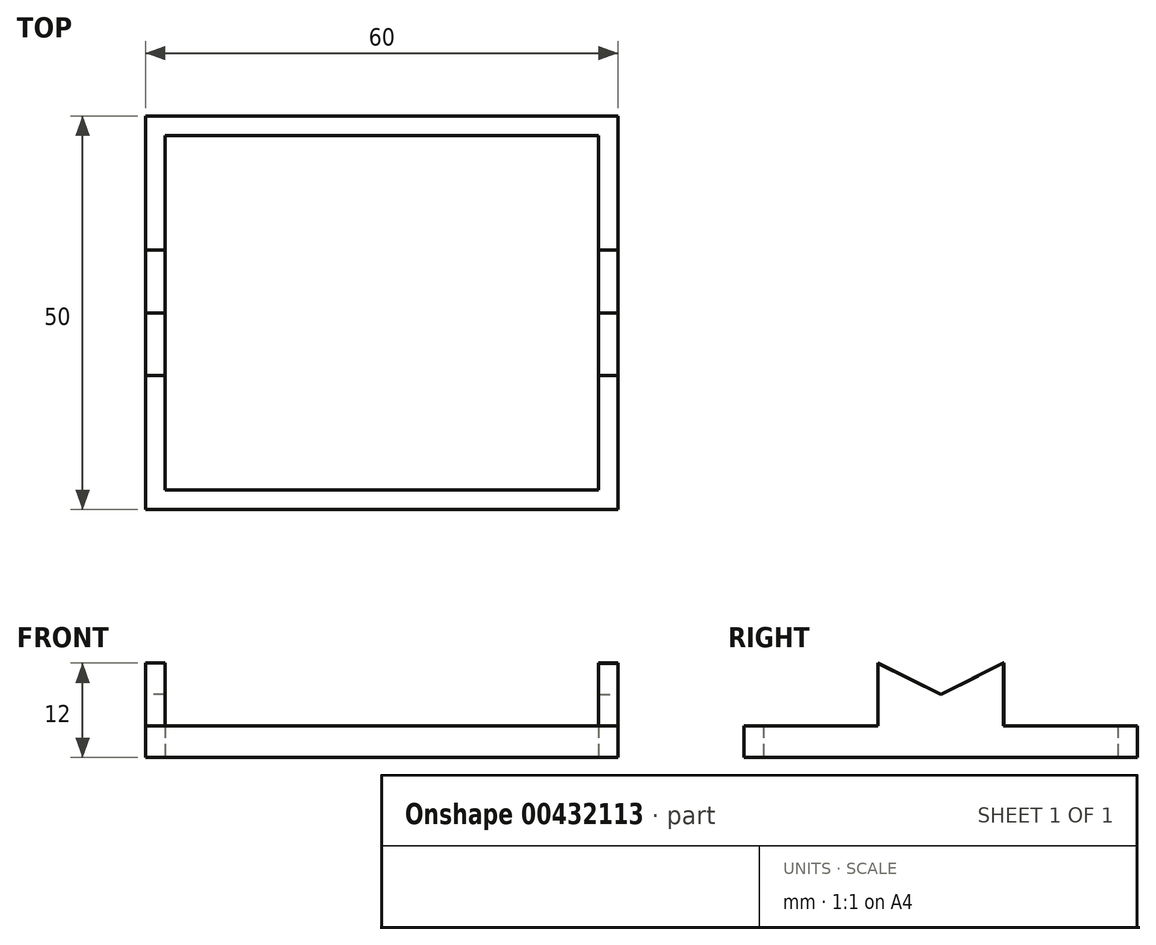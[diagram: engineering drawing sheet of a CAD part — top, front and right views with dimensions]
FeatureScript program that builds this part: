
annotation { "Feature Type Name" : "Feature", "Feature Type Description" : "" }
export const myFeature = defineFeature(function(context is Context, id is Id, definition is map)
    precondition{}
    {
        {
            var Q0;
            Q0=qCreatedBy(makeId("Top.planeOp"),FACE);
            var sketch = newSketch(context, id + "F0", { "sketchPlane" : qUnion([Q0])});
            skLineSegment(sketch, "E0.bottom", {"start": v(30, -25) * mm, "end": v(-30, -25) * mm});
            skLineSegment(sketch, "E0.top", {"start": v(30, 25) * mm, "end": v(-30, 25) * mm});
            skLineSegment(sketch, "E0.left", {"start": v(30, -25) * mm, "end": v(30, 25) * mm});
            skLineSegment(sketch, "E0.right", {"start": v(-30, -25) * mm, "end": v(-30, 25) * mm});
            skPoint(sketch, "E0.middle", {"position": v(0, 0) * mm});
            skLineSegment(sketch, "E1.bottom", {"start": v(27.5, -22.5) * mm, "end": v(-27.5, -22.5) * mm});
            skLineSegment(sketch, "E1.top", {"start": v(27.5, 22.5) * mm, "end": v(-27.5, 22.5) * mm});
            skLineSegment(sketch, "E1.left", {"start": v(27.5, -22.5) * mm, "end": v(27.5, 22.5) * mm});
            skLineSegment(sketch, "E1.right", {"start": v(-27.5, -22.5) * mm, "end": v(-27.5, 22.5) * mm});
            skSolve(sketch);
        }
        {
            var Q0;
            Q0 = qSketchRegion(id + "F0", true);
            extrude(context, id + "F1", {"entities" : qUnion([Q0]), "depth" : 4 * mm});
        }
        {
            var Q0;
            Q0=makeQuery(id+"F1.opExtrude","SWEPT_FACE",FACE,{"disambiguationData":[OSD([sQuery(id+"F0.wireOp",EDGE,"E0.right")])]});
            var sketch = newSketch(context, id + "F2", { "sketchPlane" : qUnion([Q0])});
            skLineSegment(sketch, "E2", {"start": v(0, 0) * mm, "end": v(0, 8) * mm, "construction": true});
            skPoint(sketch, "E2.endSnap0", {"position": v(0, 4) * mm});
            skLineSegment(sketch, "E3", {"start": v(0, 0) * mm, "end": v(-8, 0) * mm, "construction": true});
            skLineSegment(sketch, "E4", {"start": v(-8, 0) * mm, "end": v(-8, 12) * mm, "construction": true});
            skLineSegment(sketch, "E5.MirrorCS", {"start": v(8, 0) * mm, "end": v(8, 12) * mm, "construction": true});
            skLineSegment(sketch, "E6", {"start": v(-8, 4) * mm, "end": v(-8, 12) * mm});
            skLineSegment(sketch, "E7", {"start": v(-8, 12) * mm, "end": v(0, 8) * mm});
            skLineSegment(sketch, "E8", {"start": v(0, 8) * mm, "end": v(8, 12) * mm});
            skLineSegment(sketch, "E9", {"start": v(8, 12) * mm, "end": v(8, 4) * mm});
            skSolve(sketch);
        }
        {
            var Q0;
            Q0 = qSketchRegion(id + "F2", true);
            var Q1;
            {var subQ1=sQuery(id+"F2.wireOp",EDGE,"E6");Q1=makeQuery(id+"F2.imprint","IMPRINT",FACE,{"disambiguationData":[TD([[makeQuery(id+"F2.imprint","IMPRINT",EDGE,{"derivedFrom":subQ1}),-1.0]])]});}
            extrude(context, id + "F3", {"entities" : qUnion([Q0, Q1]), "operationType" : NewBodyOperationType.ADD, "oppositeDirection" : true, "depth" : 2.5 * mm});
        }
        {
            var Q0;
            Q0=makeQuery(id+"F1.opExtrude","SWEPT_FACE",FACE,{"disambiguationData":[OSD([sQuery(id+"F0.wireOp",EDGE,"E0.left")])]});
            var sketch = newSketch(context, id + "F4", { "sketchPlane" : qUnion([Q0])});
            skLineSegment(sketch, "E10", {"start": v(-7.98, 4) * mm, "end": v(-7.98, 11.94) * mm});
            skLineSegment(sketch, "E11", {"start": v(-7.98, 11.94) * mm, "end": v(0, 8) * mm});
            skLineSegment(sketch, "E12", {"start": v(0, 8) * mm, "end": v(8, 12) * mm});
            skLineSegment(sketch, "E13", {"start": v(8, 12) * mm, "end": v(8, 4) * mm});
            skLineSegment(sketch, "E14", {"start": v(8, 4) * mm, "end": v(-7.98, 4) * mm});
            skSolve(sketch);
        }
        {
            var Q0;
            Q0=makeQuery(id+"F4.imprint","IMPRINT",FACE,{"disambiguationData":[TD([[makeQuery(id+"F4.imprint","IMPRINT",EDGE,{"derivedFrom":sQuery(id+"F4.wireOp",EDGE,"E10")}),-1.0]])]});
            extrude(context, id + "F5", {"entities" : qUnion([Q0]), "operationType" : NewBodyOperationType.ADD, "oppositeDirection" : true, "depth" : 2.5 * mm});
        }
    });
